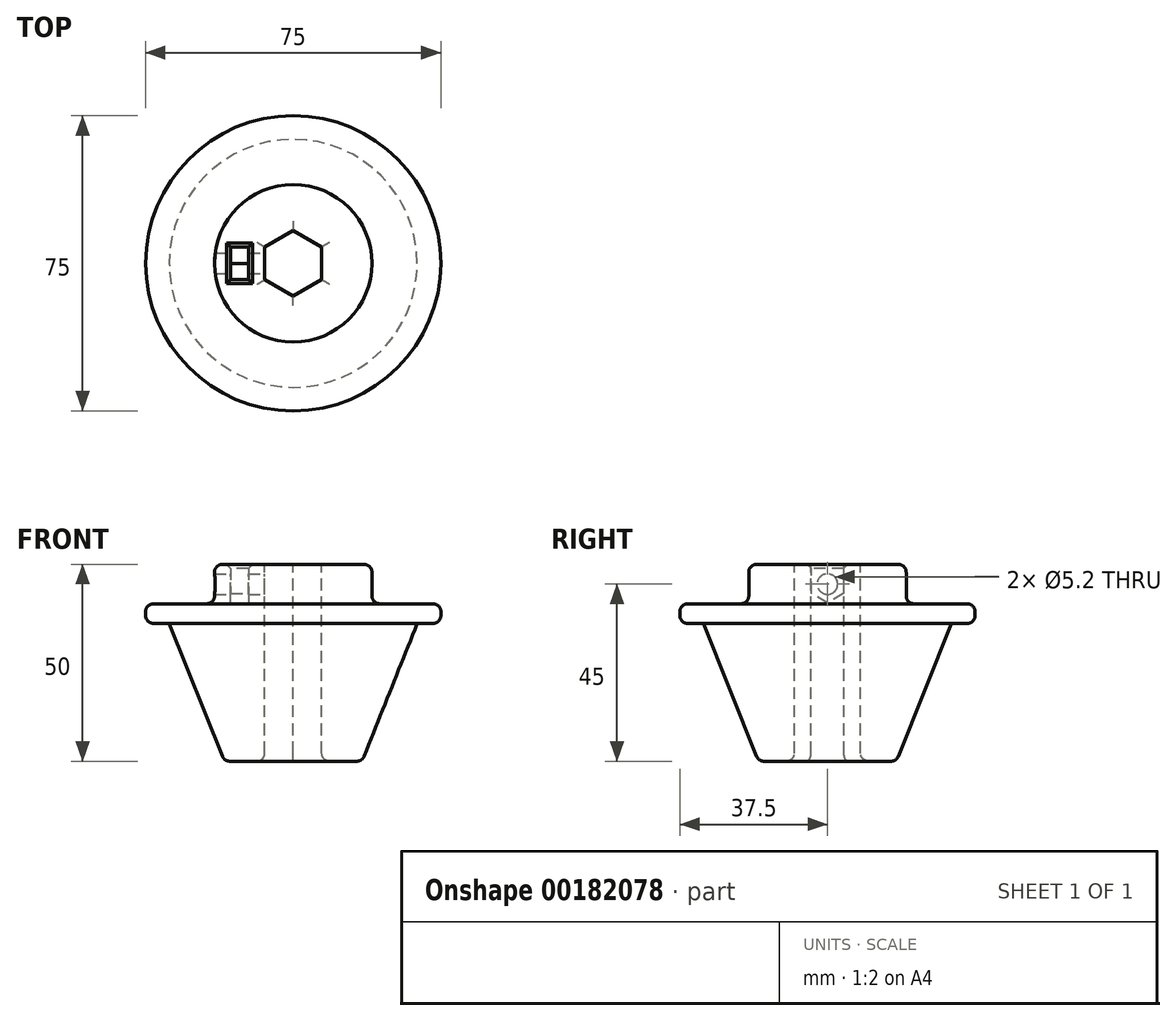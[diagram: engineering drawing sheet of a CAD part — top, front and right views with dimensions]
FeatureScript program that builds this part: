
annotation { "Feature Type Name" : "Feature", "Feature Type Description" : "" }
export const myFeature = defineFeature(function(context is Context, id is Id, definition is map)
    precondition{}
    {
        {
            var Q0;
            Q0=qCreatedBy(makeId("Front.planeOp"),FACE);
            var sketch = newSketch(context, id + "F0", { "sketchPlane" : qUnion([Q0])});
            skLineSegment(sketch, "E0", {"start": v(17.5, 0) * mm, "end": v(31.5, 35) * mm});
            skLineSegment(sketch, "E1", {"start": v(31.5, 35) * mm, "end": v(37.5, 35) * mm});
            skLineSegment(sketch, "E2", {"start": v(37.5, 35) * mm, "end": v(37.5, 40) * mm});
            skLineSegment(sketch, "E3", {"start": v(37.5, 40) * mm, "end": v(20, 40) * mm});
            skLineSegment(sketch, "E4", {"start": v(20, 40) * mm, "end": v(20, 50) * mm});
            skLineSegment(sketch, "E5", {"start": v(20, 50) * mm, "end": v(0, 50) * mm});
            skLineSegment(sketch, "E6", {"start": v(0, 50) * mm, "end": v(0, 0) * mm});
            skLineSegment(sketch, "E7", {"start": v(0, 0) * mm, "end": v(17.5, 0) * mm});
            skSolve(sketch);
        }
        {
            var Q0;
            Q0=makeQuery(id+"F0.imprint","IMPRINT",FACE,{"disambiguationData":[TD([[makeQuery(id+"F0.imprint","IMPRINT",EDGE,{"derivedFrom":sQuery(id+"F0.wireOp",EDGE,"E0")}),1.0]])]});
            var Q1;
            Q1=sQuery(id+"F0.wireOp",EDGE,"E6");
            revolve(context, id + "F1", {"entities" : qUnion([Q0]), "axis" : qUnion([Q1]), "revolveType" : RevolveType.FULL});
        }
        {
            var Q0;
            Q0=makeQuery(id+"F1.opRevolve","SWEPT_FACE",FACE,{"disambiguationData":[OSD([sQuery(id+"F0.wireOp",EDGE,"E5")])]});
            var sketch = newSketch(context, id + "F2", { "sketchPlane" : qUnion([Q0])});
            skCircle(sketch, "E8.cCircle", {"center": v(0, 0) * mm, "radius": 7.25 * mm, "construction": true});
            skLineSegment(sketch, "E8.0", {"start": v(7.25, -4.19) * mm, "end": v(0, -8.37) * mm});
            skLineSegment(sketch, "E8.1", {"start": v(0, -8.37) * mm, "end": v(-7.25, -4.19) * mm});
            skLineSegment(sketch, "E8.2", {"start": v(-7.25, -4.19) * mm, "end": v(-7.25, 4.19) * mm});
            skLineSegment(sketch, "E8.3", {"start": v(-7.25, 4.19) * mm, "end": v(0, 8.37) * mm});
            skLineSegment(sketch, "E8.4", {"start": v(0, 8.37) * mm, "end": v(7.25, 4.19) * mm});
            skLineSegment(sketch, "E8.5", {"start": v(7.25, 4.19) * mm, "end": v(7.25, -4.19) * mm});
            skPoint(sketch, "E8.0.midPoint", {"position": v(3.62, -6.28) * mm});
            skSolve(sketch);
        }
        {
            var Q0;
            Q0 = qSketchRegion(id + "F2", true);
            extrude(context, id + "F3", {"entities" : qUnion([Q0]), "operationType" : NewBodyOperationType.REMOVE, "endBound" : BoundingType.THROUGH_ALL, "oppositeDirection" : true, "depth" : 25 * mm});
        }
        {
            var Q0;
            Q0=qCreatedBy(makeId("Right.planeOp"),FACE);
            var sketch = newSketch(context, id + "F4", { "sketchPlane" : qUnion([Q0])});
            skLineSegment(sketch, "E9", {"start": v(-20, 40) * mm, "end": v(-20, 50) * mm, "construction": true});
            skLineSegment(sketch, "E10", {"start": v(20, 50) * mm, "end": v(20, 40) * mm, "construction": true});
            skLineSegment(sketch, "E11", {"start": v(20, 40) * mm, "end": v(-20, 50) * mm, "construction": true});
            skCircle(sketch, "E12", {"center": v(0, 45) * mm, "radius": 2.6 * mm});
            skCircle(sketch, "E13.cCircle", {"center": v(0, 45) * mm, "radius": 4.1 * mm, "construction": true});
            skLineSegment(sketch, "E13.0", {"start": v(-4.1, 42.63) * mm, "end": v(-4.1, 55) * mm});
            skLineSegment(sketch, "E13.1", {"start": v(-4.1, 47.37) * mm, "end": v(0, 49.73) * mm, "construction": true});
            skLineSegment(sketch, "E13.2", {"start": v(0, 49.73) * mm, "end": v(4.1, 47.37) * mm, "construction": true});
            skLineSegment(sketch, "E13.3", {"start": v(4.1, 55) * mm, "end": v(4.1, 42.63) * mm});
            skLineSegment(sketch, "E13.4", {"start": v(4.1, 42.63) * mm, "end": v(0, 40.27) * mm});
            skLineSegment(sketch, "E13.5", {"start": v(0, 40.27) * mm, "end": v(-4.1, 42.63) * mm});
            skPoint(sketch, "E13.0.midPoint", {"position": v(-4.1, 45) * mm});
            skLineSegment(sketch, "E14", {"start": v(4.1, 55) * mm, "end": v(-4.1, 55) * mm});
            skSolve(sketch);
        }
        {
            var Q0;
            Q0=makeQuery(id+"F4.imprint","IMPRINT",FACE,{"disambiguationData":[TD([[makeQuery(id+"F4.imprint","IMPRINT",EDGE,{"derivedFrom":sQuery(id+"F4.wireOp",EDGE,"E12")}),1.0]])]});
            var Q1;
            Q1=sQuery(id+"F4.wireOp",EDGE,"E12");
            extrude(context, id + "F5", {"entities" : qUnion([Q0]), "operationType" : NewBodyOperationType.REMOVE, "surfaceEntities" : qUnion([Q1]), "endBound" : BoundingType.THROUGH_ALL, "oppositeDirection" : true, "depth" : 50 * mm});
        }
        {
            var Q0;
            Q0=makeQuery(id+"F1.opRevolve","SWEPT_FACE",FACE,{"disambiguationData":[OSD([sQuery(id+"F0.wireOp",EDGE,"E5")])]});
            var sketch = newSketch(context, id + "F6", { "sketchPlane" : qUnion([Q0])});
            skLineSegment(sketch, "E15", {"start": v(-7.25, 0) * mm, "end": v(-20, 0) * mm});
            skLineSegment(sketch, "E16", {"start": v(-13.62, 0) * mm, "end": v(-13.62, -28.42) * mm, "construction": true});
            skSolve(sketch);
        }
        {
            var Q0;
            Q0=sQuery(id+"F6.wireOp",EDGE,"E16");
            cPlane(context, id + "F7", {"entities" : qUnion([Q0]), "cplaneType" : CPlaneType.LINE_ANGLE, "offset" : 25 * mm, "angle" : 90 * degree, "width" : 150 * mm, "height" : 150 * mm});
        }
        {
            var Q0;
            Q0=qCreatedBy(id+"F7.planeOp",FACE);
            var sketch = newSketch(context, id + "F8", { "sketchPlane" : qUnion([Q0])});
            skPoint(sketch, "E17.0", {"position": v(-4.1, 55) * mm});
            skLineSegment(sketch, "E17.1", {"start": v(4.1, 55) * mm, "end": v(-4.1, 55) * mm});
            skLineSegment(sketch, "E17.2", {"start": v(-4.1, 42.63) * mm, "end": v(-4.1, 55) * mm});
            skLineSegment(sketch, "E17.3", {"start": v(4.1, 55) * mm, "end": v(4.1, 42.63) * mm});
            skLineSegment(sketch, "E17.4", {"start": v(4.1, 42.63) * mm, "end": v(0, 40.27) * mm});
            skLineSegment(sketch, "E17.5", {"start": v(0, 40.27) * mm, "end": v(-4.1, 42.63) * mm});
            skSolve(sketch);
        }
        {
            var Q0;
            Q0 = qSketchRegion(id + "F8", true);
            extrude(context, id + "F9", {"entities" : qUnion([Q0]), "operationType" : NewBodyOperationType.REMOVE, "endBound" : BoundingType.SYMMETRIC, "oppositeDirection" : true, "depth" : 4.5 * mm});
        }
        {
            var Q0;
            Q0=makeQuery(id+"F1.opRevolve","SWEPT_EDGE",EDGE,{"disambiguationData":[OSD([sQuery(id+"F0.wireOp",EDGE,"E4"),sQuery(id+"F0.wireOp",EDGE,"E5")])]});
            var Q1;
            Q1=makeQuery(id+"F1.opRevolve","SWEPT_EDGE",EDGE,{"disambiguationData":[OSD([sQuery(id+"F0.wireOp",EDGE,"E3"),sQuery(id+"F0.wireOp",EDGE,"E4")])]});
            var Q2;
            Q2=makeQuery(id+"F1.opRevolve","SWEPT_EDGE",EDGE,{"disambiguationData":[OSD([sQuery(id+"F0.wireOp",EDGE,"E2"),sQuery(id+"F0.wireOp",EDGE,"E3")])]});
            var Q3;
            Q3=makeQuery(id+"F1.opRevolve","SWEPT_EDGE",EDGE,{"disambiguationData":[OSD([sQuery(id+"F0.wireOp",EDGE,"E1"),sQuery(id+"F0.wireOp",EDGE,"E2")])]});
            var Q4;
            Q4=makeQuery(id+"F1.opRevolve","SWEPT_EDGE",EDGE,{"disambiguationData":[OSD([sQuery(id+"F0.wireOp",EDGE,"E0"),sQuery(id+"F0.wireOp",EDGE,"E7")])]});
            var Q5;
            Q5=makeQuery(id+"F3.boolean.opBoolean","INTERSECT",EDGE,{"derivedFrom":[makeQuery(id+"F1.opRevolve","SWEPT_FACE",FACE,{"disambiguationData":[OSD([sQuery(id+"F0.wireOp",EDGE,"E7")])]}),makeQuery(id+"F3.opExtrude","SWEPT_FACE",FACE,{"disambiguationData":[OSD([sQuery(id+"F2.wireOp",EDGE,"E8.1")])]})]});
            var Q6;
            Q6=makeQuery(id+"F3.boolean.opBoolean","INTERSECT",EDGE,{"derivedFrom":[makeQuery(id+"F1.opRevolve","SWEPT_FACE",FACE,{"disambiguationData":[OSD([sQuery(id+"F0.wireOp",EDGE,"E7")])]}),makeQuery(id+"F3.opExtrude","SWEPT_FACE",FACE,{"disambiguationData":[OSD([sQuery(id+"F2.wireOp",EDGE,"E8.0")])]})]});
            var Q7;
            Q7=makeQuery(id+"F3.boolean.opBoolean","INTERSECT",EDGE,{"derivedFrom":[makeQuery(id+"F1.opRevolve","SWEPT_FACE",FACE,{"disambiguationData":[OSD([sQuery(id+"F0.wireOp",EDGE,"E7")])]}),makeQuery(id+"F3.opExtrude","SWEPT_FACE",FACE,{"disambiguationData":[OSD([sQuery(id+"F2.wireOp",EDGE,"E8.5")])]})]});
            var Q8;
            Q8=makeQuery(id+"F3.boolean.opBoolean","INTERSECT",EDGE,{"derivedFrom":[makeQuery(id+"F1.opRevolve","SWEPT_FACE",FACE,{"disambiguationData":[OSD([sQuery(id+"F0.wireOp",EDGE,"E7")])]}),makeQuery(id+"F3.opExtrude","SWEPT_FACE",FACE,{"disambiguationData":[OSD([sQuery(id+"F2.wireOp",EDGE,"E8.4")])]})]});
            var Q9;
            Q9=makeQuery(id+"F3.boolean.opBoolean","INTERSECT",EDGE,{"derivedFrom":[makeQuery(id+"F1.opRevolve","SWEPT_FACE",FACE,{"disambiguationData":[OSD([sQuery(id+"F0.wireOp",EDGE,"E7")])]}),makeQuery(id+"F3.opExtrude","SWEPT_FACE",FACE,{"disambiguationData":[OSD([sQuery(id+"F2.wireOp",EDGE,"E8.3")])]})]});
            var Q10;
            Q10=makeQuery(id+"F3.boolean.opBoolean","INTERSECT",EDGE,{"derivedFrom":[makeQuery(id+"F1.opRevolve","SWEPT_FACE",FACE,{"disambiguationData":[OSD([sQuery(id+"F0.wireOp",EDGE,"E7")])]}),makeQuery(id+"F3.opExtrude","SWEPT_FACE",FACE,{"disambiguationData":[OSD([sQuery(id+"F2.wireOp",EDGE,"E8.2")])]})]});
            fillet(context, id + "F10", {"entities" : qUnion([Q0, Q1, Q2, Q3, Q4, Q5, Q6, Q7, Q8, Q9, Q10]), "radius" : 2 * mm, "tangentPropagation" : true, "allowEdgeOverflow" : false});
        }
        {
            var Q0;
            Q0=makeQuery(id+"F9.boolean.opBoolean","INTERSECT",EDGE,{"derivedFrom":[makeQuery(id+"F1.opRevolve","SWEPT_FACE",FACE,{"disambiguationData":[OSD([sQuery(id+"F0.wireOp",EDGE,"E5")])]}),makeQuery(id+"F9.opExtrude","SWEPT_FACE",FACE,{"disambiguationData":[OSD([sQuery(id+"F8.wireOp",EDGE,"E17.3")])]})]});
            var Q1;
            Q1=makeQuery(id+"F9.boolean.opBoolean","INTERSECT",EDGE,{"derivedFrom":[makeQuery(id+"F1.opRevolve","SWEPT_FACE",FACE,{"disambiguationData":[OSD([sQuery(id+"F0.wireOp",EDGE,"E5")])]}),makeQuery(id+"F9.opExtrude","CAP_FACE",FACE,{"disambiguationData":[OSD([sQuery(id+"F8.wireOp",EDGE,"E17.1"),sQuery(id+"F8.wireOp",EDGE,"E17.2"),sQuery(id+"F8.wireOp",EDGE,"E17.3"),sQuery(id+"F8.wireOp",EDGE,"E17.4"),sQuery(id+"F8.wireOp",EDGE,"E17.5")])],"isStart":false})]});
            var Q2;
            Q2=makeQuery(id+"F9.boolean.opBoolean","INTERSECT",EDGE,{"derivedFrom":[makeQuery(id+"F1.opRevolve","SWEPT_FACE",FACE,{"disambiguationData":[OSD([sQuery(id+"F0.wireOp",EDGE,"E5")])]}),makeQuery(id+"F9.opExtrude","SWEPT_FACE",FACE,{"disambiguationData":[OSD([sQuery(id+"F8.wireOp",EDGE,"E17.2")])]})]});
            var Q3;
            Q3=makeQuery(id+"F9.boolean.opBoolean","INTERSECT",EDGE,{"derivedFrom":[makeQuery(id+"F1.opRevolve","SWEPT_FACE",FACE,{"disambiguationData":[OSD([sQuery(id+"F0.wireOp",EDGE,"E5")])]}),makeQuery(id+"F9.opExtrude","CAP_FACE",FACE,{"disambiguationData":[OSD([sQuery(id+"F8.wireOp",EDGE,"E17.1"),sQuery(id+"F8.wireOp",EDGE,"E17.2"),sQuery(id+"F8.wireOp",EDGE,"E17.3"),sQuery(id+"F8.wireOp",EDGE,"E17.4"),sQuery(id+"F8.wireOp",EDGE,"E17.5")])],"isStart":true})]});
            chamfer(context, id + "F11", {"entities" : qUnion([Q0, Q1, Q2, Q3]), "width" : 1 * mm, "tangentPropagation" : true});
        }
    });
